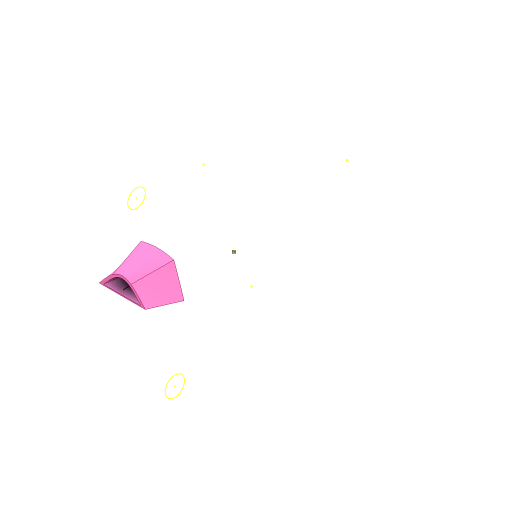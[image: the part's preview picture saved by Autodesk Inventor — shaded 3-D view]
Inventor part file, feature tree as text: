
AUTODESK INVENTOR PART (.ipt)
format: ipt  version: 2024 (Build 280153000, 153)  size: 1,546,752 bytes
history: native  units: mm
features: sketch x33, extrude x27, projected_geometry x15, split x10, other x10, boolean_combine x7, loft x6, plane x5, fillet x2, sweep x2, thicken_offset x2
ambient origin geometry x8: Origin, YZ Plane, XZ Plane, XY Plane, X Axis, Y Axis, Z Axis, Center Point
bodies: Solid1 (feature_tree), Solid2 (feature_tree), Solid19 (feature_tree), Solid21 (feature_tree), Solid22 (feature_tree), Solid23 (feature_tree), Solid24 (feature_tree), Solid3 (feature_tree), Solid4 (feature_tree), Solid5 (feature_tree), Solid6 (feature_tree), Solid7 (feature_tree), Solid8 (feature_tree), Solid9 (feature_tree), Solid10 (feature_tree), Solid11 (feature_tree), Solid12 (feature_tree), Solid13 (feature_tree), Solid14 (feature_tree), Solid15 (feature_tree), Solid16 (feature_tree), Solid17 (feature_tree), Solid18 (feature_tree)
feature tree (119):
  extrude  "Extrusion1"  Depth=9.5mm TaperAngle=0.0deg
  extrude  "Extrusion2"  Depth=3.0mm TaperAngle=0.0deg
  extrude  "Extrusion3"  Depth=40.0mm
  plane  "Work Plane2"
  sketch  "Sketch4"  dims[d4=29.0mm d5=3.0mm d6=0.0mm]
  loft  "Loft1"
  loft  "Loft2"
  loft  "Loft3"
  loft  "Loft4"
  boolean_combine  "Combine1"
  loft  "Loft5"
  fillet  "Fillet1"  [1 undecoded]
  fillet  "Fillet2"  [1 undecoded]
  plane  "Work Plane3"
  extrude  "Extrusion5"  TaperAngle=0.0deg  [1 undecoded]
  extrude  "Extrusion6"  TaperAngle=0.0deg  [1 undecoded]
  extrude  "Extrusion7"  Depth=40.0mm
  extrude  "Extrusion8"  TaperAngle=0.0deg  [1 undecoded]
  extrude  "Extrusion9"  Depth=2.0mm
  extrude  "Extrusion10"  Depth=38.0mm
  extrude  "Extrusion11"  Depth=3.0mm TaperAngle=0.0deg
  extrude  "Extrusion12"  Depth=3.0mm TaperAngle=0.0deg
  extrude  "Extrusion14"  Depth=12.5mm TaperAngle=0.0deg
  extrude  "Extrusion15"  Depth=3.7mm TaperAngle=0.0deg
  split  "Split1"
  split  "Split2"
  split  "Split3"
  split  "Split4"
  split  "Split5"
  split  "Split6"
  split  "Split7"
  boolean_combine  "Combine2"
  split  "Split8"
  boolean_combine  "Combine3"
  boolean_combine  "Combine4"
  extrude  "Extrusion16"  Depth=8.5mm
  extrude  "Extrusion17"  Depth=8.5mm
  sketch  "Sketch36"  dims[d43=1.5mm d46=38.0mm]
  sweep  "Sweep1"
  split  "Split9"
  thicken_offset  "Thicken1"
  extrude  "Extrusion18"  Depth=10.0mm
  sweep  "Sweep2"
  split  "Split10"
  thicken_offset  "Thicken2"
  boolean_combine  "Combine5"
  plane  "Work Plane4"
  extrude  "Extrusion19"  Depth=5.5mm
  other  "Work Point1"
  other  "Work Point2"
  other  "Work Point3"
  extrude  "Extrusion20"  Depth=8.5mm
  extrude  "Extrusion21"  Depth=2.5mm TaperAngle=0.0deg
  extrude  "Extrusion22"  TaperAngle=0.0deg  [1 undecoded]
  extrude  "Extrusion23"  Depth=10.0mm
  extrude  "Extrusion24"  Depth=16.5mm
  boolean_combine  "Combine6"
  plane  "Work Plane5"
  extrude  "Extrusion25"  Depth=4.0mm
  sketch  "Sketch58"  dims[d81=8.5mm d82=8.5mm]
  sketch  "Sketch59"  dims[d83=2.5mm d84=0.0mm d85=2.5mm d86=0.0mm]
  sketch  "3D Sketch4"
  extrude  "Extrusion26"  Depth=2.5mm
  boolean_combine  "Combine7"
  extrude  "Extrusion27"  Depth=2.5mm
  extrude  "Extrusion28"  Depth=5.0mm
  extrude  "Extrusion29"  Depth=5.0mm
  loft  "Loft7"
  sketch  "Sketch1"  dims[d0=3.0mm d1=0.0mm d2=9.5mm d3=0.0mm]
  plane  "Work Plane1"
  other  "2D Equation Curve1"
  other  "Edges1"
  other  "Edges2"
  other  "Edges3"
  other  "Edges4"
  sketch  "Sketch7"  dims[d7=12.0mm d8=36.0mm d9=40.0mm]
  sketch  "Sketch10"  dims[d10=9.0mm d11=10.0mm]
  sketch  "Sketch12"  dims[d12=3.0mm d13=-6.5mm d14=6.5mm]
  sketch  "Sketch13"  dims[d15=40.0mm d16=26.0mm]
  sketch  "Sketch16"  dims[d17=20.0mm d18=20.0mm]
  projected_geometry  "Projected Loop1"
  sketch  "Sketch19"  dims[d19=0.0mm d20=90.0deg d21=0.0mm d22=90.0deg d23=0.0mm d24=90.0deg d25=0.0mm d26=90.0deg]
  projected_geometry  "Projected Loop2"
  projected_geometry  "Projected Loop3"
  projected_geometry  "Projected Loop4"
  projected_geometry  "Projected Loop5"
  sketch  "Sketch23"  dims[d27=0.0mm d28=90.0deg d29=0.0mm d30=90.0deg]
  sketch  "Sketch24"  dims[d31=0.0mm d32=90.0deg d33=0.0mm d34=90.0deg]
  sketch  "Sketch28"  dims[d35=26.0mm d36=40.0mm]
  sketch  "Sketch29"  dims[d37=4.0mm d38=0.0mm d39=90.0deg]
  sketch  "Sketch35"  dims[d40=0.0mm d41=90.0deg d42=2.0mm]
  projected_geometry  "Projected Loop11"
  sketch  "3D Sketch2"
  other  "Srf1"
  sketch  "Sketch38"  dims[d47=15.0mm d48=3.0mm d49=0.0mm]
  projected_geometry  "Projected Loop12"
  sketch  "Sketch46"  dims[d50=15.0mm d51=3.0mm d52=0.0mm]
  projected_geometry  "Projected Loop21"
  sketch  "3D Sketch3"
  sketch  "Sketch47"  dims[d53=11.0mm d54=12.5mm d55=0.0mm]
  projected_geometry  "Projected Loop22"
  sketch  "Sketch49"  dims[d56=11.0mm d57=3.7mm d58=0.0mm]
  sketch  "Sketch50"  dims[d59=20.0mm d60=0.0mm d61=8.5mm]
  sketch  "Sketch52"  dims[d62=8.5mm d63=8.5mm]
  sketch  "Sketch53"  dims[d64=8.5mm d65=2.7mm d66=0.0mm]
  projected_geometry  "Projected Loop25"
  projected_geometry  "Projected Loop26"
  sketch  "Sketch54"  dims[d67=40.0mm d68=10.0mm]
  sketch  "Sketch56"  dims[d69=2.7mm d70=0.0mm d71=2.5mm d72=0.0mm]
  sketch  "Sketch57"  dims[d73=2.5mm d74=0.0mm d80=5.5mm]
  sketch  "Sketch60"  dims[d87=0.5mm d88=0.0mm d89=0.0mm]
  sketch  "Sketch61"  dims[d91=10.0mm d92=10.0mm]
  projected_geometry  "Projected Loop27"
  sketch  "Sketch62"  dims[d93=0.1mm d94=0.0mm d95=16.5mm]
  projected_geometry  "Projected Loop28"
  projected_geometry  "Projected Loop29"
  sketch  "Sketch63"  dims[d96=2.5mm d97=4.0mm d98=2.5mm d99=2.5mm d100=5.0mm d101=5.0mm d102=2.5mm d103=2.5mm d104=2.5mm d105=2.5mm d106=0.0mm d107=0.0mm d108=2.5mm d109=2.5mm d114=0.1mm d115=0.1mm d116=0.1mm d117=0.0mm d118=15.0mm d119=3.0mm d120=1.6mm d121=1.5mm d122=16.5mm d125=5.5mm d126=2.5mm d127=2.5mm d128=0.0mm d129=0.0mm d130=0.1mm d131=0.1mm d132=58.25mm d133=6.0mm d134=16.0mm d135=0.0mm d136=12.0mm d137=12.0mm d138=12.0mm d139=12.0mm d140=10.0mm d141=0.0mm d142=0.0mm d143=0.0mm d144=0.0mm d145=0.0mm d146=0.0mm d147=0.0mm d148=9.273806mm d149=9.273806mm d150=0.0mm d151=0.0mm d152=-10.0mm d153=0.0mm d154=0.0mm d155=11.0mm d156=0.0mm d157=4.75mm d158=0.0mm d159=0.0mm d160=0.0mm d161=4.0mm d162=0.0mm d163=0.0mm d164=90.0deg d165=0.0mm d166=90.0deg d110=0.5mm d111=0.872665mm d112=0.5mm d113=0.872665mm]
  projected_geometry  "Projected Loop30"
  other  "Unwrap1"
note: 6 required parameter values undecoded (feature->parameter linkage not recoverable at this tier; creation-order binding heuristic only, values carry confidence <= 0.55)
